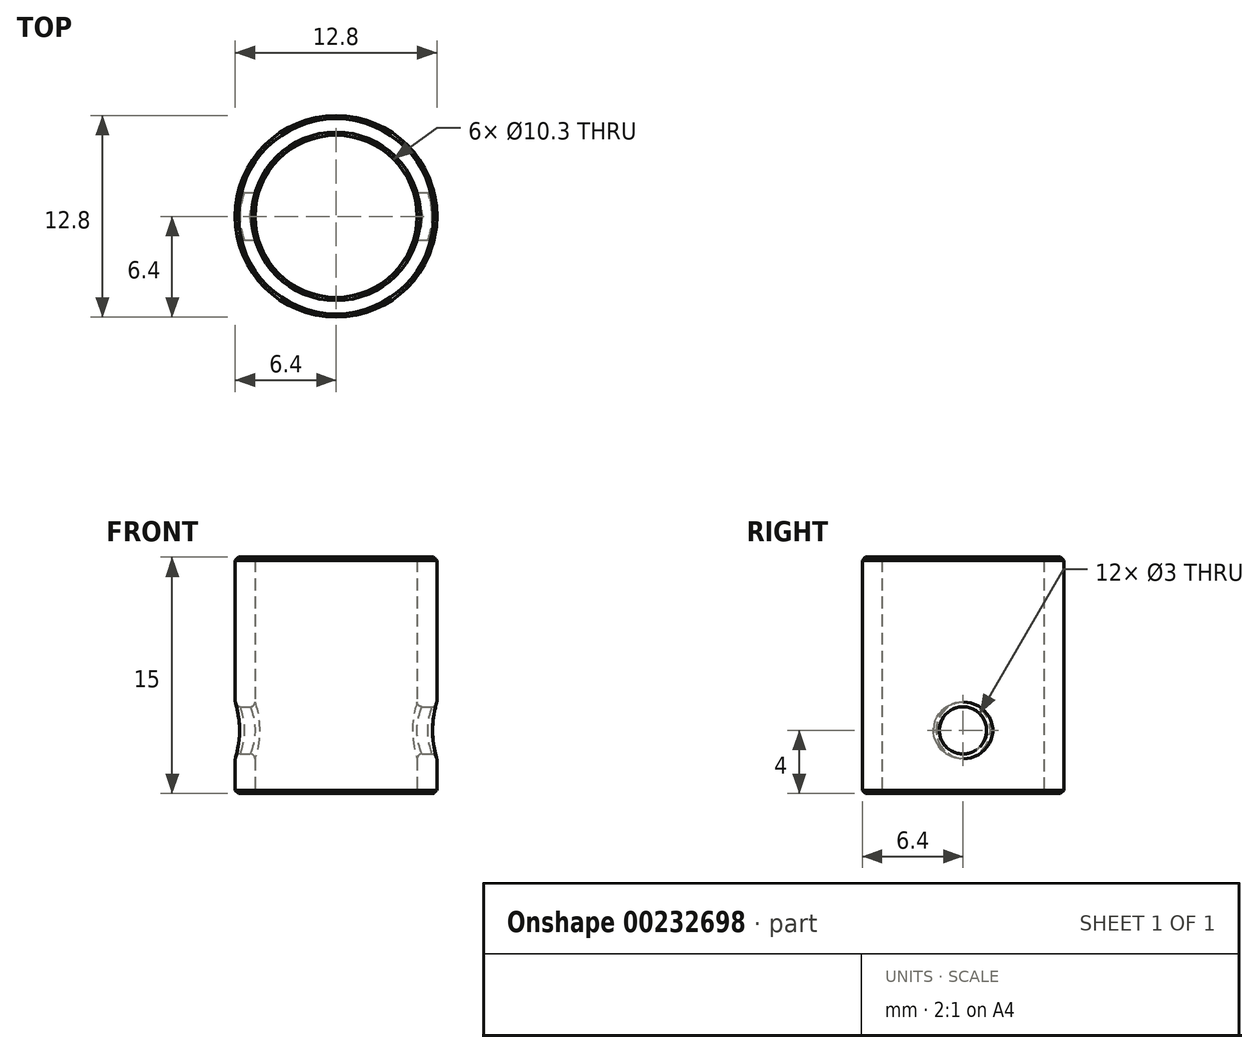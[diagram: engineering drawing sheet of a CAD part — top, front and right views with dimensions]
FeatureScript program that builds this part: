
annotation { "Feature Type Name" : "Feature", "Feature Type Description" : "" }
export const myFeature = defineFeature(function(context is Context, id is Id, definition is map)
    precondition{}
    {
        {
            var Q0;
            Q0=qCreatedBy(makeId("Top.planeOp"),FACE);
            var sketch = newSketch(context, id + "F0", { "sketchPlane" : qUnion([Q0])});
            skCircle(sketch, "E0", {"center": v(0, 0) * mm, "radius": 6.4 * mm});
            skCircle(sketch, "E1", {"center": v(0, 0) * mm, "radius": 5.15 * mm});
            skSolve(sketch);
        }
        {
            var Q0;
            Q0 = qSketchRegion(id + "F0", true);
            extrude(context, id + "F1", {"entities" : qUnion([Q0]), "depth" : 15 * mm});
        }
        {
            var Q0;
            Q0=qCreatedBy(makeId("Right.planeOp"),FACE);
            var sketch = newSketch(context, id + "F2", { "sketchPlane" : qUnion([Q0])});
            skCircle(sketch, "E2", {"center": v(0, 4) * mm, "radius": 1.5 * mm});
            skSolve(sketch);
        }
        {
            var Q0;
            Q0 = qSketchRegion(id + "F2", true);
            extrude(context, id + "F3", {"entities" : qUnion([Q0]), "operationType" : NewBodyOperationType.REMOVE, "endBound" : BoundingType.SYMMETRIC, "oppositeDirection" : true, "depth" : 550 * mm});
        }
        {
            var Q0;
            Q0=makeQuery(id+"F3.boolean.opBoolean","INTERSECT",EDGE,{"disambiguationData":[OD(1.0)],"derivedFrom":[makeQuery(id+"F1.opExtrude","SWEPT_FACE",FACE,{"disambiguationData":[OSD([sQuery(id+"F0.wireOp",EDGE,"E0")])]}),makeQuery(id+"F3.opExtrude","SWEPT_FACE",FACE,{"disambiguationData":[OSD([sQuery(id+"F2.wireOp",EDGE,"E2")])]})]});
            var Q1;
            Q1=makeQuery(id+"F3.boolean.opBoolean","INTERSECT",EDGE,{"disambiguationData":[OD(1.0)],"derivedFrom":[makeQuery(id+"F1.opExtrude","SWEPT_FACE",FACE,{"disambiguationData":[OSD([sQuery(id+"F0.wireOp",EDGE,"E1")])]}),makeQuery(id+"F3.opExtrude","SWEPT_FACE",FACE,{"disambiguationData":[OSD([sQuery(id+"F2.wireOp",EDGE,"E2")])]})]});
            var Q2;
            Q2=makeQuery(id+"F3.boolean.opBoolean","INTERSECT",EDGE,{"disambiguationData":[OD(0.0)],"derivedFrom":[makeQuery(id+"F1.opExtrude","SWEPT_FACE",FACE,{"disambiguationData":[OSD([sQuery(id+"F0.wireOp",EDGE,"E1")])]}),makeQuery(id+"F3.opExtrude","SWEPT_FACE",FACE,{"disambiguationData":[OSD([sQuery(id+"F2.wireOp",EDGE,"E2")])]})]});
            var Q3;
            Q3=makeQuery(id+"F3.boolean.opBoolean","INTERSECT",EDGE,{"disambiguationData":[OD(0.0)],"derivedFrom":[makeQuery(id+"F1.opExtrude","SWEPT_FACE",FACE,{"disambiguationData":[OSD([sQuery(id+"F0.wireOp",EDGE,"E0")])]}),makeQuery(id+"F3.opExtrude","SWEPT_FACE",FACE,{"disambiguationData":[OSD([sQuery(id+"F2.wireOp",EDGE,"E2")])]})]});
            fillet(context, id + "F4", {"entities" : qUnion([Q0, Q1, Q2, Q3]), "radius" : .3 * mm, "tangentPropagation" : true, "allowEdgeOverflow" : false});
        }
        {
            var Q0;
            Q0=makeQuery(id+"F1.opExtrude","CAP_EDGE",EDGE,{"disambiguationData":[OSD([sQuery(id+"F0.wireOp",EDGE,"E0")])],"isStart":false});
            var Q1;
            Q1=makeQuery(id+"F1.opExtrude","CAP_FACE",FACE,{"disambiguationData":[OSD([sQuery(id+"F0.wireOp",EDGE,"E0"),sQuery(id+"F0.wireOp",EDGE,"E1")])],"isStart":false});
            var Q2;
            Q2=makeQuery(id+"F1.opExtrude","CAP_FACE",FACE,{"disambiguationData":[OSD([sQuery(id+"F0.wireOp",EDGE,"E0"),sQuery(id+"F0.wireOp",EDGE,"E1")])],"isStart":true});
            chamfer(context, id + "F5", {"entities" : qUnion([Q0, Q1, Q2]), "width" : .2 * mm, "tangentPropagation" : true});
        }
    });
